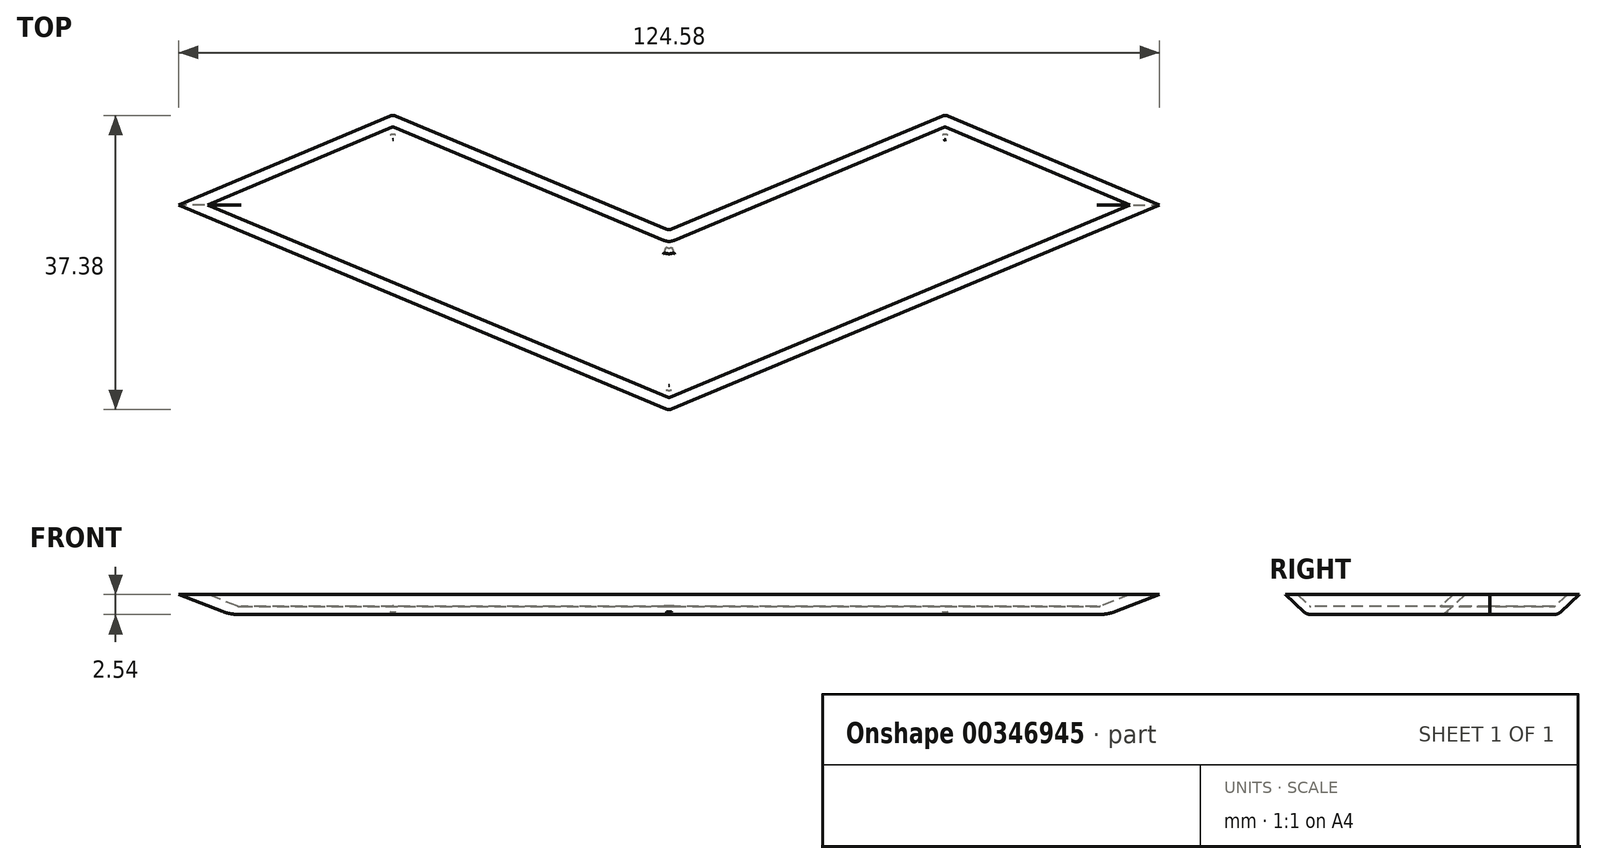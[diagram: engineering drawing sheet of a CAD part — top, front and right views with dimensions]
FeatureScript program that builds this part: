
annotation { "Feature Type Name" : "Feature", "Feature Type Description" : "" }
export const myFeature = defineFeature(function(context is Context, id is Id, definition is map)
    precondition{}
    {
        {
            var Q0;
            Q0=qCreatedBy(makeId("Top.planeOp"),FACE);
            var Q1;
            Q1=qCreatedBy(makeId("Top.planeOp"),FACE);
            var Q2;
            Q2=qCreatedBy(makeId("Top.planeOp"),FACE);
            var sketch = newSketch(context, id + "F0", { "sketchPlane" : qUnion([Q0, Q1, Q2])});
            skLineSegment(sketch, "E0", {"start": v(0, 0) * mm, "end": v(46.72, 19.52) * mm});
            skLineSegment(sketch, "E1", {"start": v(46.72, 19.52) * mm, "end": v(62.29, 26.03) * mm});
            skLineSegment(sketch, "E2", {"start": v(62.29, 26.03) * mm, "end": v(35.08, 37.52) * mm});
            skLineSegment(sketch, "E3.MirrorCS", {"start": v(0, 0) * mm, "end": v(-46.72, 19.52) * mm});
            skLineSegment(sketch, "E4.MirrorCS", {"start": v(-46.72, 19.52) * mm, "end": v(-62.29, 26.03) * mm});
            skLineSegment(sketch, "E5.MirrorCS", {"start": v(-62.29, 26.03) * mm, "end": v(-35.08, 37.52) * mm});
            skLineSegment(sketch, "E6", {"start": v(35.08, 37.52) * mm, "end": v(0, 22.86) * mm});
            skLineSegment(sketch, "E7", {"start": v(-35.08, 37.52) * mm, "end": v(0, 22.86) * mm});
            skSolve(sketch);
        }
        {
            var Q0;
            Q0=makeQuery(id+"F0.imprint","IMPRINT",FACE,{"disambiguationData":[TD([[makeQuery(id+"F0.imprint","IMPRINT",EDGE,{"derivedFrom":sQuery(id+"F0.wireOp",EDGE,"E0")}),1.0]])]});
            extrude(context, id + "F1", {"entities" : qUnion([Q0]), "depth" : 2.54 * mm});
        }
        {
            var Q0;
            Q0=makeQuery(id+"F1.opExtrude","CAP_FACE",FACE,{"disambiguationData":[OSD([sQuery(id+"F0.wireOp",EDGE,"E0"),sQuery(id+"F0.wireOp",EDGE,"d0j5HF9T-eNUY-yKca-Yy7e-2Wkt3A4gEZQK"),sQuery(id+"F0.wireOp",EDGE,"TnYXo5uh-Zz5f-UBdW-j2td-FpZNfwGPwua1"),sQuery(id+"F0.wireOp",EDGE,"c7834862-45bb-44c2-94f3-8f2a4d2a01710.MirrorCS"),sQuery(id+"F0.wireOp",EDGE,"c30a79c2-4364-4fa4-b31f-7d8688597f0d0.MirrorCS"),sQuery(id+"F0.wireOp",EDGE,"2750f083-4f45-4423-8a3c-d1f4f3610ced0.MirrorCS")])],"isStart":true});
            var Q1;
            Q1=makeQuery(id+"F1.opExtrude","CAP_FACE",FACE,{"disambiguationData":[OSD([sQuery(id+"F0.wireOp",EDGE,"E0"),sQuery(id+"F0.wireOp",EDGE,"d0j5HF9T-eNUY-yKca-Yy7e-2Wkt3A4gEZQK"),sQuery(id+"F0.wireOp",EDGE,"TnYXo5uh-Zz5f-UBdW-j2td-FpZNfwGPwua1"),sQuery(id+"F0.wireOp",EDGE,"c7834862-45bb-44c2-94f3-8f2a4d2a01710.MirrorCS"),sQuery(id+"F0.wireOp",EDGE,"c30a79c2-4364-4fa4-b31f-7d8688597f0d0.MirrorCS"),sQuery(id+"F0.wireOp",EDGE,"2750f083-4f45-4423-8a3c-d1f4f3610ced0.MirrorCS")])],"isStart":true});
            chamfer(context, id + "F2", {"entities" : qUnion([Q0, Q1]), "width" : 2.54 * mm, "tangentPropagation" : true});
        }
        {
            var Q0;
            Q0=makeQuery(id+"F2.opChamfer","BLEND_EDGE",EDGE,{"blendedFrom":[makeQuery(id+"F1.opExtrude","CAP_EDGE",EDGE,{"disambiguationData":[OSD([sQuery(id+"F0.wireOp",EDGE,"E6")])],"isStart":true}),makeQuery(id+"F1.opExtrude","CAP_EDGE",EDGE,{"disambiguationData":[OSD([sQuery(id+"F0.wireOp",EDGE,"E7")])],"isStart":true})],"blendedInto":[]});
            var Q1;
            Q1=makeQuery(id+"F1.opExtrude","CAP_FACE",FACE,{"disambiguationData":[OSD([sQuery(id+"F0.wireOp",EDGE,"E0"),sQuery(id+"F0.wireOp",EDGE,"E1"),sQuery(id+"F0.wireOp",EDGE,"E2"),sQuery(id+"F0.wireOp",EDGE,"E3.MirrorCS"),sQuery(id+"F0.wireOp",EDGE,"E4.MirrorCS"),sQuery(id+"F0.wireOp",EDGE,"E5.MirrorCS"),sQuery(id+"F0.wireOp",EDGE,"E6"),sQuery(id+"F0.wireOp",EDGE,"E7")])],"isStart":true});
            var Q2;
            Q2=makeQuery(id+"F2.opChamfer","BLEND_EDGE",EDGE,{"blendedFrom":[makeQuery(id+"F1.opExtrude","CAP_EDGE",EDGE,{"disambiguationData":[OSD([sQuery(id+"F0.wireOp",EDGE,"E2")])],"isStart":true}),makeQuery(id+"F1.opExtrude","CAP_EDGE",EDGE,{"disambiguationData":[OSD([sQuery(id+"F0.wireOp",EDGE,"E6")])],"isStart":true})],"blendedInto":[]});
            var Q3;
            Q3=makeQuery(id+"F2.opChamfer","BLEND_EDGE",EDGE,{"blendedFrom":[makeQuery(id+"F1.opExtrude","CAP_EDGE",EDGE,{"disambiguationData":[OSD([sQuery(id+"F0.wireOp",EDGE,"E0"),sQuery(id+"F0.wireOp",EDGE,"E1")])],"isStart":true}),makeQuery(id+"F1.opExtrude","CAP_EDGE",EDGE,{"disambiguationData":[OSD([sQuery(id+"F0.wireOp",EDGE,"E3.MirrorCS"),sQuery(id+"F0.wireOp",EDGE,"E4.MirrorCS")])],"isStart":true})],"blendedInto":[]});
            var Q4;
            Q4=makeQuery(id+"F2.opChamfer","BLEND_EDGE",EDGE,{"blendedFrom":[makeQuery(id+"F1.opExtrude","CAP_EDGE",EDGE,{"disambiguationData":[OSD([sQuery(id+"F0.wireOp",EDGE,"E5.MirrorCS")])],"isStart":true}),makeQuery(id+"F1.opExtrude","CAP_EDGE",EDGE,{"disambiguationData":[OSD([sQuery(id+"F0.wireOp",EDGE,"E7")])],"isStart":true})],"blendedInto":[]});
            fillet(context, id + "F3", {"entities" : qUnion([Q0, Q1, Q2, Q3, Q4]), "radius" : 1.27 * mm, "tangentPropagation" : true, "allowEdgeOverflow" : false});
        }
        {
            var Q0;
            Q0=makeQuery(id+"F1.opExtrude","CAP_FACE",FACE,{"disambiguationData":[OSD([sQuery(id+"F0.wireOp",EDGE,"E0"),sQuery(id+"F0.wireOp",EDGE,"E1"),sQuery(id+"F0.wireOp",EDGE,"E2"),sQuery(id+"F0.wireOp",EDGE,"E3.MirrorCS"),sQuery(id+"F0.wireOp",EDGE,"E4.MirrorCS"),sQuery(id+"F0.wireOp",EDGE,"E5.MirrorCS"),sQuery(id+"F0.wireOp",EDGE,"E6"),sQuery(id+"F0.wireOp",EDGE,"E7")])],"isStart":false});
            shell(context, id + "F4", {"entities" : qUnion([Q0]), "thickness" : 1.02 * mm});
        }
    });
